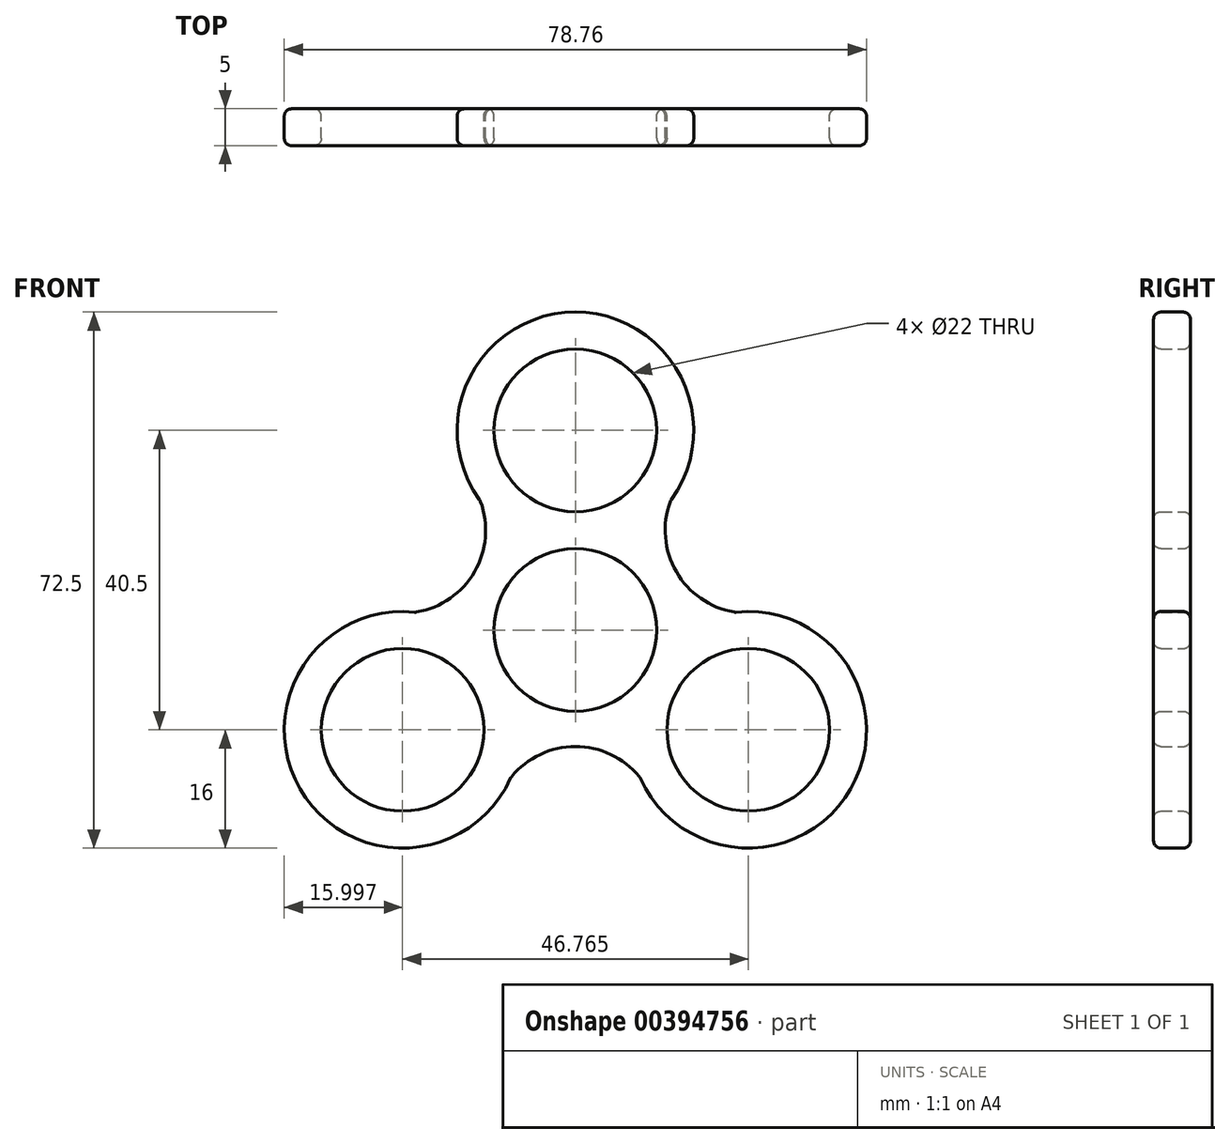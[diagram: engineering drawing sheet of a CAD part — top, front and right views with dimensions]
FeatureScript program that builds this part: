
annotation { "Feature Type Name" : "Feature", "Feature Type Description" : "" }
export const myFeature = defineFeature(function(context is Context, id is Id, definition is map)
    precondition{}
    {
        {
            var Q0;
            Q0=qCreatedBy(makeId("Front.planeOp"),FACE);
            var sketch = newSketch(context, id + "F0", { "sketchPlane" : qUnion([Q0])});
            skCircle(sketch, "E0", {"center": v(0, 0) * mm, "radius": 11 * mm});
            skCircle(sketch, "E1", {"center": v(0, 0) * mm, "radius": 16 * mm, "construction": true});
            skLineSegment(sketch, "E2", {"start": v(0, 0) * mm, "end": v(0, 27) * mm, "construction": true});
            skCircle(sketch, "E3", {"center": v(0, 27) * mm, "radius": 11 * mm});
            skCircle(sketch, "E4", {"center": v(0, 27) * mm, "radius": 16 * mm, "construction": true});
            skLineSegment(sketch, "E5", {"start": v(0, 0) * mm, "end": v(-23.38, -13.5) * mm, "construction": true});
            skLineSegment(sketch, "E6", {"start": v(0, 0) * mm, "end": v(23.38, -13.5) * mm, "construction": true});
            skCircle(sketch, "E7", {"center": v(-23.38, -13.5) * mm, "radius": 11 * mm});
            skCircle(sketch, "E8", {"center": v(23.38, -13.5) * mm, "radius": 11 * mm});
            skCircle(sketch, "E9", {"center": v(23.38, -13.5) * mm, "radius": 16 * mm, "construction": true});
            skCircle(sketch, "E10", {"center": v(-23.38, -13.5) * mm, "radius": 16 * mm, "construction": true});
            skLineSegment(sketch, "E11", {"start": v(0, 0) * mm, "end": v(-12.89, 17.52) * mm, "construction": true});
            skLineSegment(sketch, "E12", {"start": v(0, 0) * mm, "end": v(-21.62, 2.4) * mm, "construction": true});
            skLineSegment(sketch, "E13", {"start": v(0, 0) * mm, "end": v(12.89, 17.52) * mm, "construction": true});
            skLineSegment(sketch, "E14", {"start": v(0, 0) * mm, "end": v(21.62, 2.4) * mm, "construction": true});
            skLineSegment(sketch, "E15", {"start": v(0, 0) * mm, "end": v(8.73, -19.92) * mm, "construction": true});
            skLineSegment(sketch, "E16", {"start": v(0, 0) * mm, "end": v(-8.73, -19.92) * mm, "construction": true});
            skArc(sketch, "E17", {"start": v(-21.62, 2.4) * mm, "mid": v(-37.24, -21.5) * mm, "end": v(-8.73, -19.92) * mm});
            skArc(sketch, "E18", {"start": v(8.73, -19.92) * mm, "mid": v(37.24, -21.5) * mm, "end": v(21.62, 2.4) * mm});
            skArc(sketch, "E19", {"start": v(12.89, 17.52) * mm, "mid": v(0, 43) * mm, "end": v(-12.89, 17.52) * mm});
            skLineSegment(sketch, "E20", {"start": v(0, 0) * mm, "end": v(12.89, 9.48) * mm, "construction": true});
            skLineSegment(sketch, "E21", {"start": v(0, 0) * mm, "end": v(1.77, -15.9) * mm, "construction": true});
            skLineSegment(sketch, "E22", {"start": v(0, 0) * mm, "end": v(-12.89, 9.48) * mm, "construction": true});
            skArc(sketch, "E23", {"start": v(-21.62, 2.4) * mm, "mid": v(-13.65, 7.88) * mm, "end": v(-12.89, 17.52) * mm});
            skArc(sketch, "E24", {"start": v(12.89, 17.52) * mm, "mid": v(13.65, 7.88) * mm, "end": v(21.62, 2.4) * mm});
            skArc(sketch, "E25", {"start": v(8.73, -19.92) * mm, "mid": v(0, -15.76) * mm, "end": v(-8.73, -19.92) * mm});
            skSolve(sketch);
        }
        {
            var Q0;
            Q0 = qSketchRegion(id + "F0", true);
            extrude(context, id + "F1", {"entities" : qUnion([Q0]), "depth" : 5 * mm});
        }
        {
            var Q0;
            Q0=makeQuery(id+"F1.opExtrude","SWEPT_FACE",FACE,{"disambiguationData":[OSD([sQuery(id+"F0.wireOp",EDGE,"E0")])]});
            fillet(context, id + "F2", {"entities" : qUnion([Q0]), "radius" : 1 * mm, "tangentPropagation" : true, "allowEdgeOverflow" : false});
        }
        {
            var Q0;
            Q0=makeQuery(id+"F1.opExtrude","SWEPT_FACE",FACE,{"disambiguationData":[OSD([sQuery(id+"F0.wireOp",EDGE,"E3")])]});
            fillet(context, id + "F3", {"entities" : qUnion([Q0]), "radius" : 1 * mm, "tangentPropagation" : true, "allowEdgeOverflow" : false});
        }
        {
            var Q0;
            Q0=makeQuery(id+"F1.opExtrude","SWEPT_FACE",FACE,{"disambiguationData":[OSD([sQuery(id+"F0.wireOp",EDGE,"E8")])]});
            fillet(context, id + "F4", {"entities" : qUnion([Q0]), "radius" : 1 * mm, "tangentPropagation" : true, "allowEdgeOverflow" : false});
        }
        {
            var Q0;
            Q0=makeQuery(id+"F1.opExtrude","SWEPT_FACE",FACE,{"disambiguationData":[OSD([sQuery(id+"F0.wireOp",EDGE,"E7")])]});
            fillet(context, id + "F5", {"entities" : qUnion([Q0]), "radius" : 1 * mm, "tangentPropagation" : true, "allowEdgeOverflow" : false});
        }
        {
            var Q0;
            Q0=makeQuery(id+"F1.opExtrude","SWEPT_FACE",FACE,{"disambiguationData":[OSD([sQuery(id+"F0.wireOp",EDGE,"E17")])]});
            var Q1;
            Q1=makeQuery(id+"F1.opExtrude","SWEPT_FACE",FACE,{"disambiguationData":[OSD([sQuery(id+"F0.wireOp",EDGE,"E25")])]});
            var Q2;
            Q2=makeQuery(id+"F1.opExtrude","SWEPT_FACE",FACE,{"disambiguationData":[OSD([sQuery(id+"F0.wireOp",EDGE,"E18")])]});
            var Q3;
            Q3=makeQuery(id+"F1.opExtrude","SWEPT_FACE",FACE,{"disambiguationData":[OSD([sQuery(id+"F0.wireOp",EDGE,"E24")])]});
            var Q4;
            Q4=makeQuery(id+"F1.opExtrude","SWEPT_FACE",FACE,{"disambiguationData":[OSD([sQuery(id+"F0.wireOp",EDGE,"E19")])]});
            var Q5;
            Q5=makeQuery(id+"F1.opExtrude","SWEPT_FACE",FACE,{"disambiguationData":[OSD([sQuery(id+"F0.wireOp",EDGE,"E23")])]});
            fillet(context, id + "F6", {"entities" : qUnion([Q0, Q1, Q2, Q3, Q4, Q5]), "radius" : 1 * mm, "tangentPropagation" : true, "allowEdgeOverflow" : false});
        }
    });
